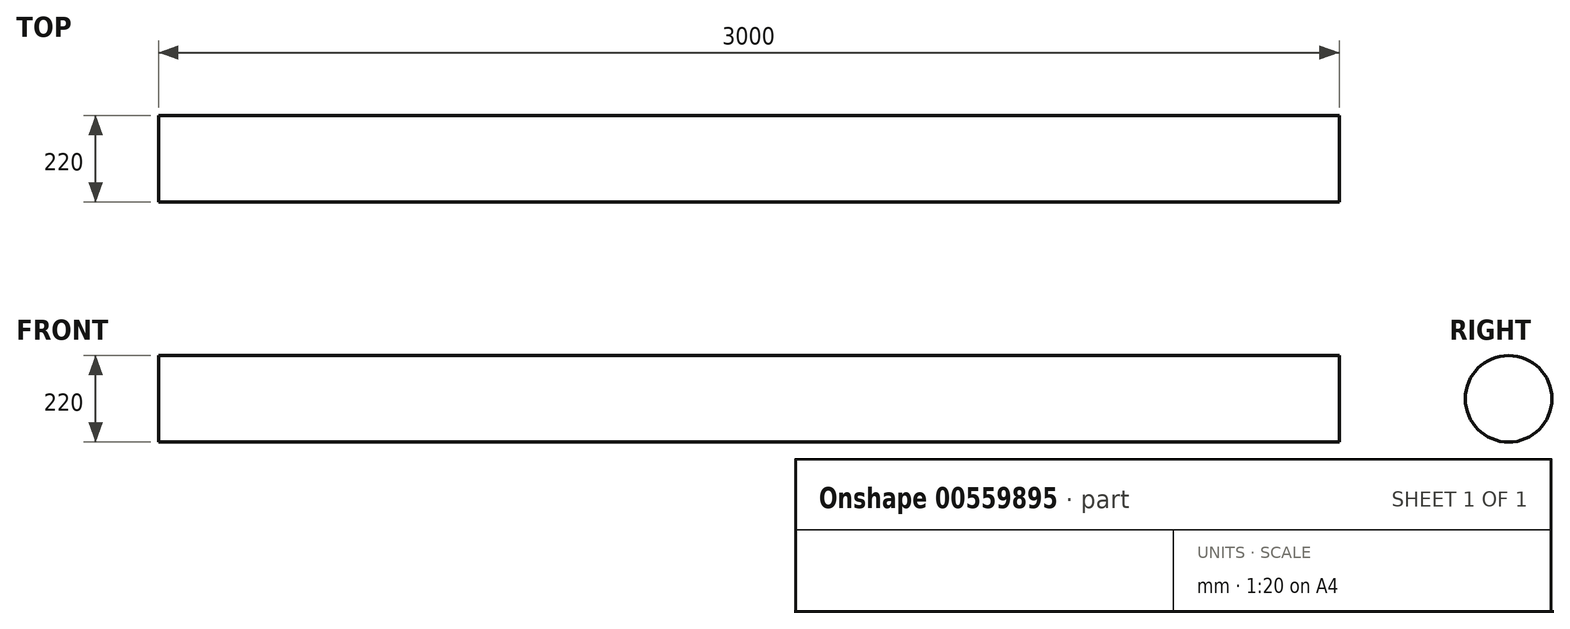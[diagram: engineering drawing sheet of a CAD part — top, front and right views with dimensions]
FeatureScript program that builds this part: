
annotation { "Feature Type Name" : "Feature", "Feature Type Description" : "" }
export const myFeature = defineFeature(function(context is Context, id is Id, definition is map)
    precondition{}
    {
        {
            var Q0;
            Q0=qCreatedBy(makeId("Right.planeOp"),FACE);
            var sketch = newSketch(context, id + "F0", { "sketchPlane" : qUnion([Q0])});
            skCircle(sketch, "E0", {"center": v(0, 0) * mm, "radius": 110 * mm});
            skSolve(sketch);
        }
        {
            var Q0;
            Q0 = qSketchRegion(id + "F0", true);
            extrude(context, id + "F1", {"entities" : qUnion([Q0]), "depth" : 3000 * mm, "offsetDistance" : 25 * mm});
        }
    });
